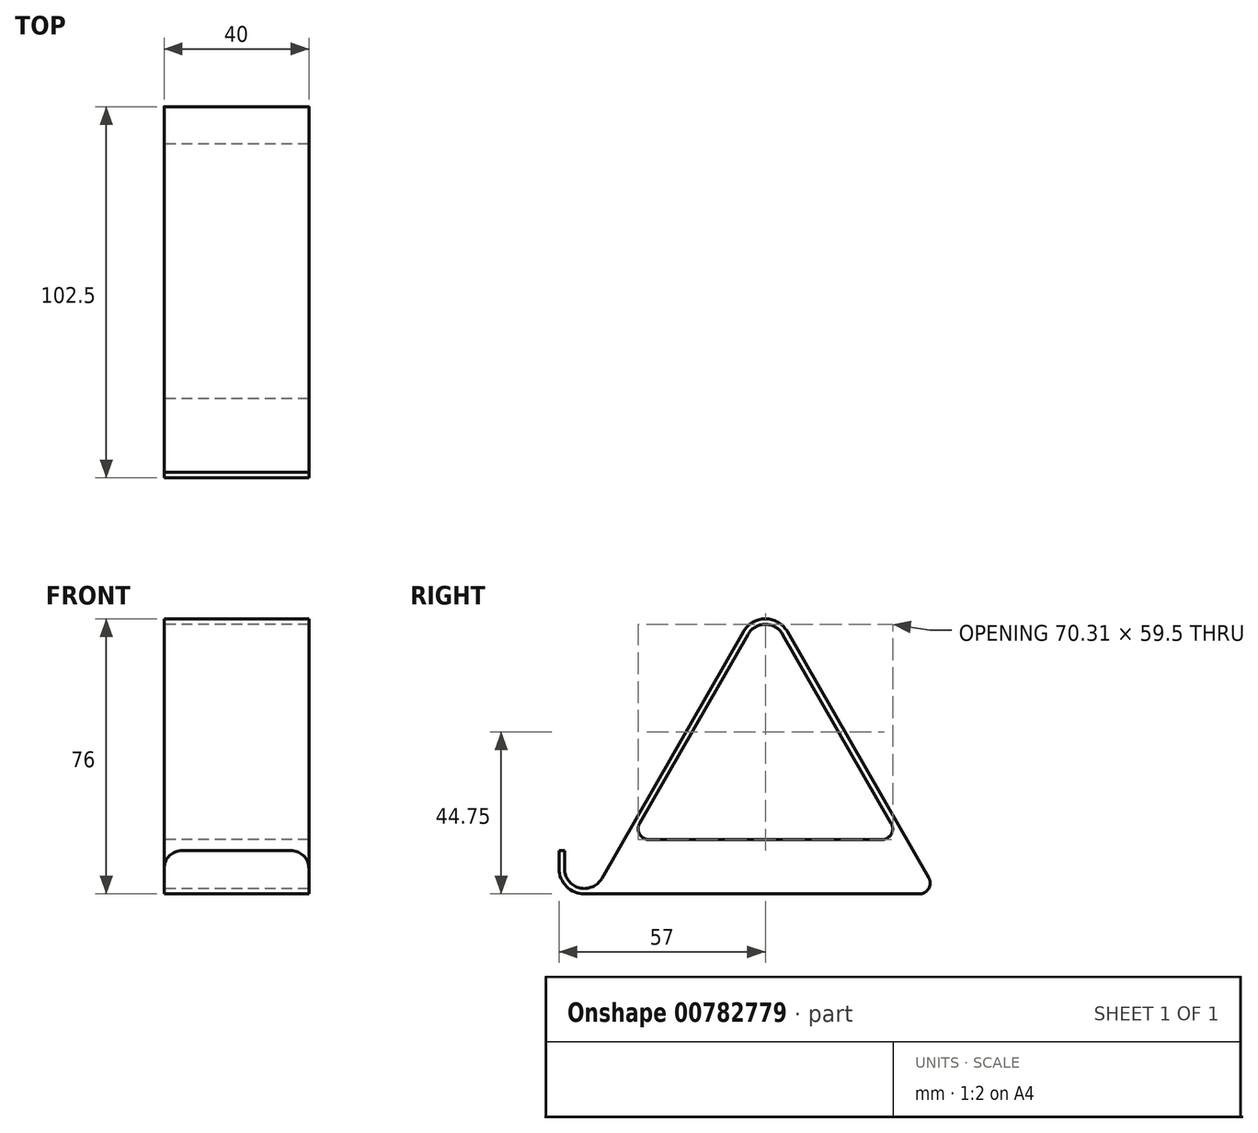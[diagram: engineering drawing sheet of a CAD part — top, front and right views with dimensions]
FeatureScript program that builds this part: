
annotation { "Feature Type Name" : "Feature", "Feature Type Description" : "" }
export const myFeature = defineFeature(function(context is Context, id is Id, definition is map)
    precondition{}
    {
        {
            var Q0;
            Q0=qCreatedBy(makeId("Right.planeOp"),FACE);
            var sketch = newSketch(context, id + "F0", { "sketchPlane" : qUnion([Q0])});
            skArc(sketch, "E0", {"start": v(-7, 0) * mm, "mid": v(-4.95, -4.95) * mm, "end": v(0, -7) * mm});
            skArc(sketch, "E1", {"start": v(54.77, 64.74) * mm, "mid": v(50, 67.5) * mm, "end": v(45.23, 64.74) * mm});
            skLineSegment(sketch, "E2", {"start": v(15.24, 12.5) * mm, "end": v(45.23, 64.74) * mm});
            skLineSegment(sketch, "E3", {"start": v(50, 62) * mm, "end": v(50, -56.8) * mm, "construction": true});
            skLineSegment(sketch, "E4", {"start": v(0, -7) * mm, "end": v(118.61, -7) * mm, "construction": true});
            skPoint(sketch, "E5.orphan", {"position": v(93.93, -3.48) * mm});
            skLineSegment(sketch, "E6", {"start": v(-7, 0) * mm, "end": v(-7, 5) * mm});
            skLineSegment(sketch, "E7.0", {"start": v(95.1, -2.5) * mm, "end": v(56.07, 65.48) * mm});
            skLineSegment(sketch, "E7.1", {"start": v(-5.5, 0) * mm, "end": v(-5.5, 5) * mm});
            skArc(sketch, "E7.2", {"start": v(-5.5, 0) * mm, "mid": v(-1.42, -5.31) * mm, "end": v(4.77, -2.74) * mm});
            skLineSegment(sketch, "E7.3", {"start": v(4.77, -2.74) * mm, "end": v(43.93, 65.48) * mm});
            skArc(sketch, "E7.4", {"start": v(56.07, 65.48) * mm, "mid": v(50, 69) * mm, "end": v(43.93, 65.48) * mm});
            skLineSegment(sketch, "E8", {"start": v(-7, 5) * mm, "end": v(-5.5, 5) * mm});
            skLineSegment(sketch, "E9", {"start": v(0, -7) * mm, "end": v(92.5, -7) * mm});
            skLineSegment(sketch, "E10.0", {"start": v(17.84, 8) * mm, "end": v(82.16, 8) * mm});
            skPoint(sketch, "E11.orphan", {"position": v(6.07, -3.48) * mm});
            skLineSegment(sketch, "E12.trimOffspring", {"start": v(84.76, 12.5) * mm, "end": v(54.77, 64.74) * mm});
            skPoint(sketch, "E13.visualSharp", {"position": v(12.66, 8) * mm});
            skArc(sketch, "E13.filletArc", {"start": v(15.24, 12.5) * mm, "mid": v(15.25, 9.5) * mm, "end": v(17.84, 8) * mm});
            skPoint(sketch, "E14.visualSharp", {"position": v(87.34, 8) * mm});
            skArc(sketch, "E14.filletArc", {"start": v(82.16, 8) * mm, "mid": v(84.75, 9.5) * mm, "end": v(84.76, 12.5) * mm});
            skLineSegment(sketch, "E15", {"start": v(0, -7) * mm, "end": v(97.68, -7) * mm});
            skPoint(sketch, "E16.visualSharp", {"position": v(97.68, -7) * mm});
            skArc(sketch, "E16.filletArc", {"start": v(92.5, -7) * mm, "mid": v(95.1, -5.5) * mm, "end": v(95.1, -2.5) * mm});
            skSolve(sketch);
        }
        {
            var Q0;
            {var subQ0=sQuery(id+"F0.wireOp",EDGE,"E0");Q0=makeQuery(id+"F0.imprint","IMPRINT",FACE,{"disambiguationData":[TD([[makeQuery(id+"F0.imprint","IMPRINT",EDGE,{"derivedFrom":subQ0}),1.0]])]});}
            extrude(context, id + "F1", {"entities" : qUnion([Q0]), "depth" : 40 * mm, "offsetDistance" : 25 * mm});
        }
        {
            var Q0;
            Q0=makeQuery(id+"F1.opExtrude","CAP_EDGE",EDGE,{"disambiguationData":[OSD([sQuery(id+"F0.wireOp",EDGE,"E8")])],"isStart":false});
            fillet(context, id + "F2", {"entities" : qUnion([Q0]), "radius" : 5 * mm, "tangentPropagation" : true, "allowEdgeOverflow" : false});
        }
        {
            var Q0;
            Q0=makeQuery(id+"F1.opExtrude","CAP_EDGE",EDGE,{"disambiguationData":[OSD([sQuery(id+"F0.wireOp",EDGE,"E8")])],"isStart":true});
            fillet(context, id + "F3", {"entities" : qUnion([Q0]), "radius" : 5 * mm, "tangentPropagation" : true, "allowEdgeOverflow" : false});
        }
    });
